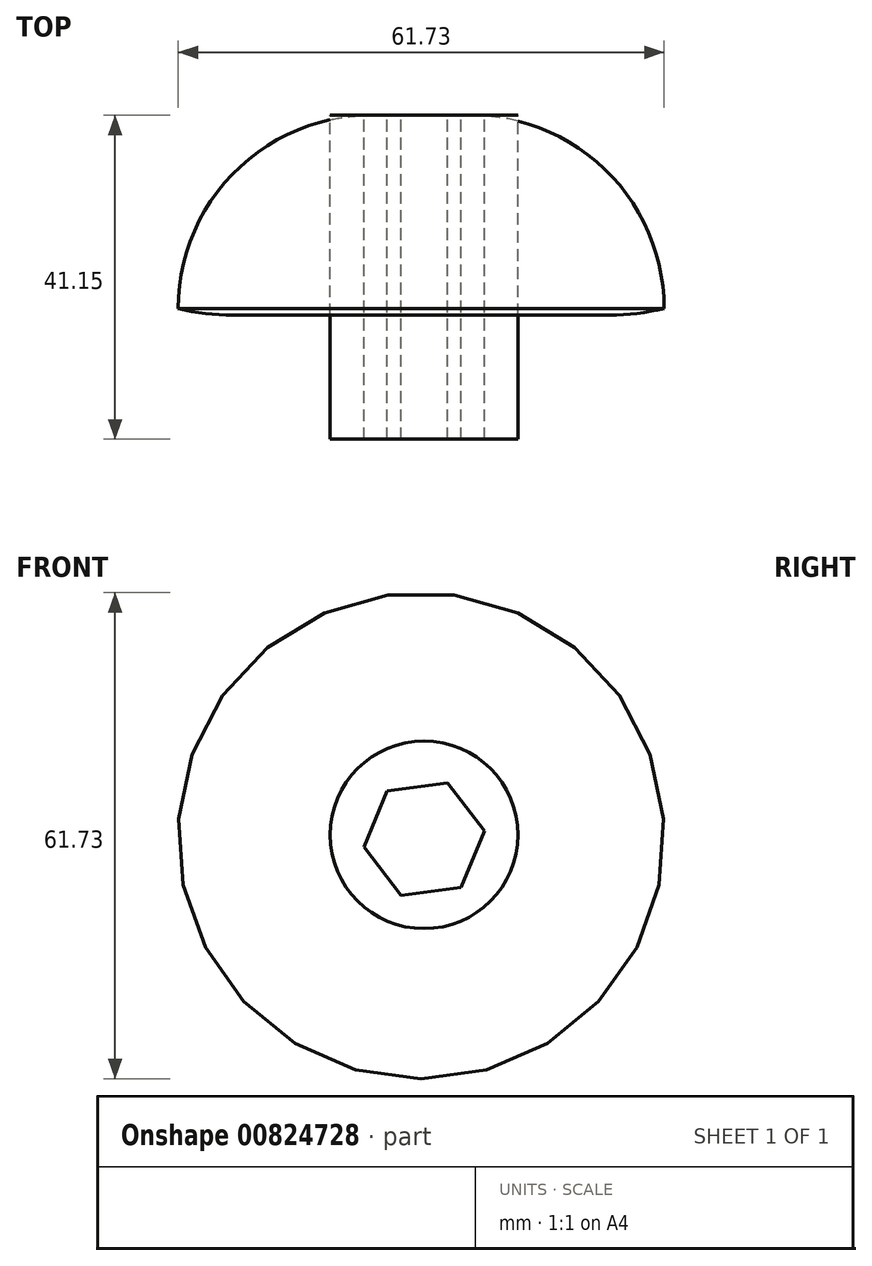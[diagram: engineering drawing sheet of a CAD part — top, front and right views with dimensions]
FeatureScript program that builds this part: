
annotation { "Feature Type Name" : "Feature", "Feature Type Description" : "" }
export const myFeature = defineFeature(function(context is Context, id is Id, definition is map)
    precondition{}
    {
        {
            var Q0;
            Q0=qCreatedBy(makeId("Front.planeOp"),FACE);
            var sketch = newSketch(context, id + "F0", { "sketchPlane" : qUnion([Q0])});
            skCircle(sketch, "E0.cCircle", {"center": v(-36.11, 2.55) * mm, "radius": 6.68 * mm, "construction": true});
            skLineSegment(sketch, "E0.0", {"start": v(-28.46, 3.57) * mm, "end": v(-31.4, -3.57) * mm});
            skLineSegment(sketch, "E0.1", {"start": v(-31.4, -3.57) * mm, "end": v(-39.06, -4.58) * mm});
            skLineSegment(sketch, "E0.2", {"start": v(-39.06, -4.58) * mm, "end": v(-43.76, 1.54) * mm});
            skLineSegment(sketch, "E0.3", {"start": v(-43.76, 1.54) * mm, "end": v(-40.81, 8.67) * mm});
            skLineSegment(sketch, "E0.4", {"start": v(-40.81, 8.67) * mm, "end": v(-33.17, 9.68) * mm});
            skLineSegment(sketch, "E0.5", {"start": v(-33.17, 9.68) * mm, "end": v(-28.46, 3.57) * mm});
            skPoint(sketch, "E0.0.midPoint", {"position": v(-29.94, 0) * mm});
            skSolve(sketch);
        }
        {
            var Q0;
            Q0=qCreatedBy(makeId("Front.planeOp"),FACE);
            var sketch = newSketch(context, id + "F1", { "sketchPlane" : qUnion([Q0])});
            skCircle(sketch, "E1", {"center": v(-36.11, 3.09) * mm, "radius": 11.92 * mm});
            skSolve(sketch);
        }
        {
            var Q0;
            Q0=makeQuery(id+"F0.imprint","IMPRINT",FACE,{"disambiguationData":[TD([[makeQuery(id+"F0.imprint","IMPRINT",EDGE,{"derivedFrom":sQuery(id+"F0.wireOp",EDGE,"E0.0")}),-1.0]])]});
            var Q1;
            Q1=makeQuery(id+"F1.imprint","IMPRINT",FACE,{"disambiguationData":[TD([[makeQuery(id+"F1.imprint","IMPRINT",EDGE,{"derivedFrom":sQuery(id+"F1.wireOp",EDGE,"E1")}),1.0]])]});
            extrude(context, id + "F2", {"entities" : qUnion([Q0, Q1]), "depth" : 41.15 * mm, "offsetDistance" : 25.4 * mm});
        }
        {
            var Q0;
            Q0=qCreatedBy(makeId("Front.planeOp"),FACE);
            var sketch = newSketch(context, id + "F3", { "sketchPlane" : qUnion([Q0])});
            skCircle(sketch, "E2", {"center": v(-36.49, 2.98) * mm, "radius": 30.86 * mm});
            skSolve(sketch);
        }
        {
            var Q0;
            Q0=makeQuery(id+"F3.imprint","IMPRINT",FACE,{"disambiguationData":[TD([[makeQuery(id+"F3.imprint","IMPRINT",EDGE,{"derivedFrom":sQuery(id+"F3.wireOp",EDGE,"E2")}),1.0]])]});
            extrude(context, id + "F4", {"entities" : qUnion([Q0]), "depth" : 25.4 * mm, "offsetDistance" : 25.4 * mm});
        }
        {
            var Q0;
            Q0=makeQuery(id+"F4.opExtrude","CAP_FACE",FACE,{"disambiguationData":[OSD([sQuery(id+"F3.wireOp",EDGE,"E2")])],"isStart":true});
            fillet(context, id + "F5", {"entities" : qUnion([Q0]), "radius" : 24.53 * mm, "tangentPropagation" : true, "allowEdgeOverflow" : false});
        }
        {
            var Q0;
            Q0=makeQuery(id+"F4.opExtrude","CAP_FACE",FACE,{"disambiguationData":[OSD([sQuery(id+"F3.wireOp",EDGE,"E2")])],"isStart":false});
            fillet(context, id + "F6", {"entities" : qUnion([Q0]), "radius" : 28.82 * mm, "tangentPropagation" : true, "rho" : 0.5, "crossSection" : FilletCrossSection.CONIC, "allowEdgeOverflow" : false});
        }
    });
